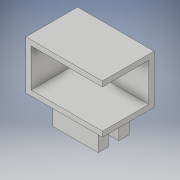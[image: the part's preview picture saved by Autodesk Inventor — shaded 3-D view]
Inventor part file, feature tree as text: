
AUTODESK INVENTOR PART (.ipt)
format: ipt  version: 2019 (Build 230136000, 136)  size: 347,136 bytes
history: native  units: in
note: dims shown in document units (in); Inventor stores cm internally (conversion verified against a paired STEP export)
features: extrude x8, sketch x8, projected_geometry x2
ambient origin geometry x8: Origin, YZ Plane, XZ Plane, XY Plane, X Axis, Y Axis, Z Axis, Center Point
bodies: Solid1 (feature_tree)
feature tree (18):
  extrude  "Extrusion1"  Depth=0.1969in
  extrude  "Extrusion2"  Depth=0.5906in
  extrude  "Extrusion3"  Depth=1.0827in TaperAngle=0.0deg
  extrude  "Extrusion4"  Depth=0.0984in
  extrude  "Extrusion5"  Depth=0.0984in
  extrude  "Extrusion6"  Depth=0.689in
  extrude  "Extrusion7"  Depth=0.2165in
  extrude  "Extrusion8"  Depth=0.3937in TaperAngle=0.0deg
  sketch  "Sketch1"  dims[d0=0.4921in d2=0.1969in]
  sketch  "Sketch2"  dims[d3=0.5906in d4=0.5906in]
  sketch  "Sketch3"  dims[d5=0.1969in d6=1.0827in d7=0.0in]
  sketch  "Sketch4"  dims[d8=0.8268in d9=0.0984in]
  sketch  "Sketch5"  dims[d10=1.5551in d11=0.0984in]
  sketch  "Sketch6"  dims[d12=0.7283in d13=0.689in]
  sketch  "Sketch7"  dims[d14=1.0827in d15=0.0in d16=0.2165in]
  projected_geometry  "Projected Loop2"
  sketch  "Sketch8"  dims[d17=0.5906in d18=0.3937in d19=0.0in d20=0.0984in d21=0.0in d22=1.3583in d23=1.3583in d24=0.0984in d25=0.0in d26=0.0984in d27=0.0in d28=0.0984in d29=0.3937in d30=0.0in d31=0.7283in d32=0.1969in d33=0.0in]
  projected_geometry  "Projected Loop3"
